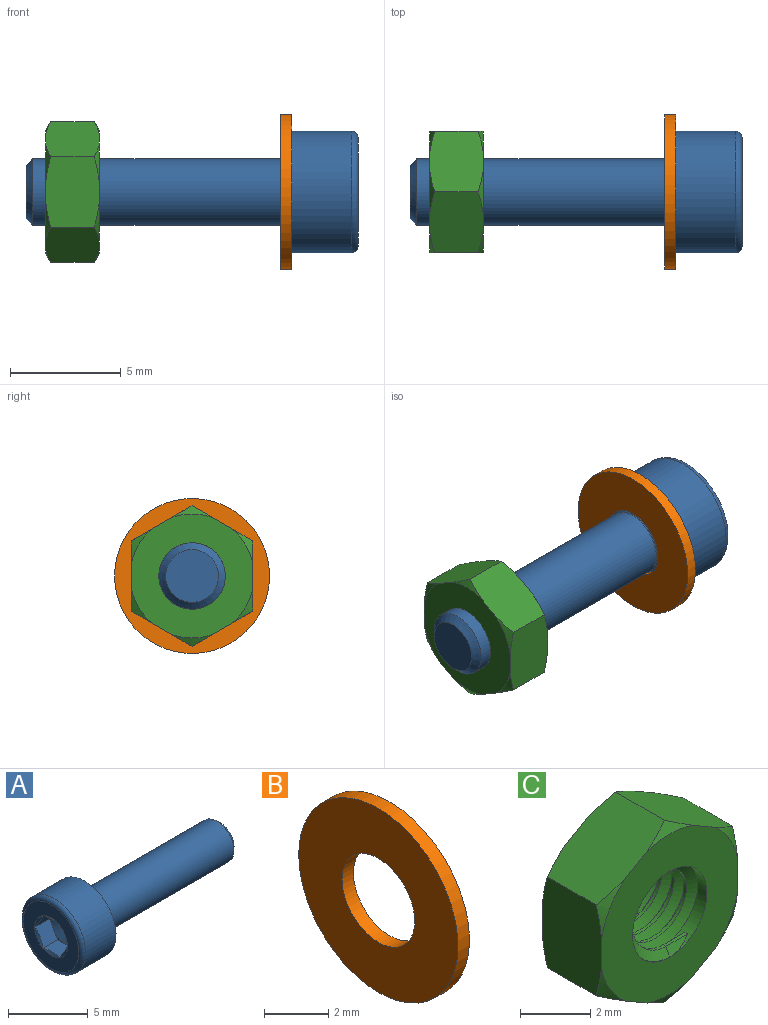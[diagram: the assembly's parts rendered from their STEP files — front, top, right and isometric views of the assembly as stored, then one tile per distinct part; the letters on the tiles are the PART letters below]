
ASSEMBLY  parts=3 mates=2
PART A: 24 faces, bbox 15x6x6 mm
  f0: plane 1.08x0.63mm, normal (-1,0,0), area 0.1mm2, adj f16,f17,f23
  f1: plane 1.25x0.36mm, normal (-1,0,0), area 0.1mm2, adj f17,f18,f23
  f2: plane 1.08x0.63mm, normal (-1,0,0), area 0.1mm2, adj f18,f19,f23
  f3: plane 1.08x0.63mm, normal (-1,0,0), area 0.1mm2, adj f19,f20,f23
  f4: plane 1.25x0.36mm, normal (-1,0,0), area 0.1mm2, adj f20,f21,f23
  f5: cone r=1.45mm half-angle=60deg, axis (-1,0,0), area 1.4mm2, adj f15,f16,f17,f18,f19,f20,f21
  f6: cone r=1.51mm half-angle=26deg, axis (-1,0,0), area 4.6mm2, adj f7,f11
  f7: torus R=1.6mm, axis (1,0,0), area 0.4mm2, adj f6,f10
  f8: plane 2.39x2.39mm, normal (1,0,0), area 4.5mm2, adj f9
  f9: cone r=1.5mm half-angle=45deg, axis (-1,0,0), area 3.7mm2, adj f8,f10
  f10: cylinder r=1.5mm len=11.18mm, axis (1,0,0), area 105.4mm2, adj f7,f9
  f11: torus R=1.8mm, axis (1,0,0), area 1.2mm2, adj f6,f13
  f12: cylinder r=2.75mm len=5.5mm, axis (1,0,0), area 46.7mm2, adj f13,f14
  f13: plane 5.5x5.5mm, normal (1,0,0), area 13.6mm2, adj f11,f12
  f14: torus R=2.45mm, axis (1,0,0), area 7.8mm2, adj f12,f15
  f15: plane 4.9x4.9mm, normal (-1,0,0), area 12.2mm2, adj f5,f14
  f16: plane 1.45x1.3mm, normal (0,0,-1), area 1.8mm2, adj f0,f5,f17,f21,f22
  f17: plane 1.29x1.25mm, normal (0,0.87,-0.5), area 1.8mm2, adj f0,f1,f5,f16,f18
  f18: plane 1.29x1.25mm, normal (0,0.87,0.5), area 1.8mm2, adj f1,f2,f5,f17,f19
  f19: plane 1.45x1.3mm, normal (0,0,1), area 1.8mm2, adj f2,f3,f5,f18,f20
  f20: plane 1.29x1.25mm, normal (0,-0.87,0.5), area 1.8mm2, adj f3,f4,f5,f19,f21
  f21: plane 1.29x1.25mm, normal (0,-0.87,-0.5), area 1.8mm2, adj f4,f5,f16,f20,f22
  f22: plane 1.08x0.63mm, normal (-1,0,0), area 0.1mm2, adj f16,f21,f23
  f23: cone r=1.25mm half-angle=60deg, axis (-1,0,0), area 5.7mm2, adj f0,f1,f2,f3,f4,f22
PART B: 4 faces, bbox 0.5x7x7 mm
  f0: plane 7x7mm, normal (-1,0,0), area 30.4mm2, adj f1,f3
  f1: cylinder r=1.6mm len=3.2mm, axis (1,0,0), area 5mm2, adj f0,f2
  f2: plane 7x7mm, normal (1,0,0), area 30.4mm2, adj f1,f3
  f3: cylinder r=3.5mm len=7mm, axis (1,0,0), area 11mm2, adj f0,f2
PART C: 28 faces, bbox 6.4x2.6x6.5 mm
  f0: cone r=2.8mm half-angle=60deg, axis (0,-1,0), area 0.4mm2, adj f11,f22,f23
  f1: cone r=2.8mm half-angle=60deg, axis (0,-1,0), area 0.4mm2, adj f11,f23,f24
  f2: cone r=2.8mm half-angle=60deg, axis (0,-1,0), area 0.4mm2, adj f11,f24,f25
  f3: cone r=2.8mm half-angle=60deg, axis (0,-1,0), area 0.4mm2, adj f11,f25,f26
  f4: cone r=2.8mm half-angle=60deg, axis (0,-1,0), area 0.4mm2, adj f11,f22,f27
  f5: cone r=3.18mm half-angle=60deg, axis (0,1,0), area 0.4mm2, adj f10,f22,f23
  f6: cone r=3.18mm half-angle=60deg, axis (0,1,0), area 0.4mm2, adj f10,f23,f24
  f7: cone r=3.18mm half-angle=60deg, axis (0,1,0), area 0.4mm2, adj f10,f24,f25
  f8: cone r=3.18mm half-angle=60deg, axis (0,1,0), area 0.4mm2, adj f10,f25,f26
  f9: cone r=3.18mm half-angle=60deg, axis (0,1,0), area 0.4mm2, adj f10,f26,f27
  f10: plane 5.6x5.5mm, normal (0,-1,0), area 17.4mm2, adj f5,f6,f7,f8,f9,f12,f21,f22
  f11: plane 5.6x5.5mm, normal (0,1,0), area 17.4mm2, adj f0,f1,f2,f3,f4,f12,f20,f22
  f12: cylinder r=1.5mm len=3mm, axis (0,1,0), area 6mm2, adj f10,f11,f13,f15,f16,f17,f18,f19
  f13: plane 0.44x0.25mm, normal (-0.88,0,-0.48), area 0.1mm2, adj f12,f14,f15,f16
  f14: cylinder r=1.21mm len=2.43mm, axis (0,1,0), area 3.3mm2, adj f13,f15,f16,f17
  f15: bspline ~3.46x3mm, area 11mm2, adj f12,f13,f14,f18
  f16: bspline ~3.46x3mm, area 11mm2, adj f12,f13,f14,f19
  f17: plane 0.88x0.11mm, normal (0,0,1), area 0.1mm2, adj f12,f14,f18,f19
  f18: plane 0.96x0.37mm, normal (0,0.87,0.5), area 0.2mm2, adj f12,f15,f17
  f19: plane 0.96x0.37mm, normal (0,-0.87,0.5), area 0.2mm2, adj f12,f16,f17
  f20: cone r=2.8mm half-angle=60deg, axis (0,-1,0), area 0.4mm2, adj f11,f26,f27
  f21: cone r=3.18mm half-angle=60deg, axis (0,1,0), area 0.4mm2, adj f10,f22,f27
  f22: plane 2.87x2.52mm, normal (-0.5,0,0.87), area 7.2mm2, adj f0,f4,f5,f10,f11,f21,f23,f27
  f23: plane 2.87x2.52mm, normal (0.5,0,0.87), area 7.2mm2, adj f0,f1,f5,f6,f10,f11,f22,f24
  f24: plane 3.3x2.52mm, normal (1,0,0), area 7.2mm2, adj f1,f2,f6,f7,f10,f11,f23,f25
  f25: plane 2.87x2.52mm, normal (0.5,0,-0.87), area 7.2mm2, adj f2,f3,f7,f8,f10,f11,f24,f26
  f26: plane 2.87x2.52mm, normal (-0.5,0,-0.87), area 7.2mm2, adj f3,f8,f9,f10,f11,f20,f25,f27
  f27: plane 3.3x2.52mm, normal (-1,0,0), area 7.2mm2, adj f4,f9,f10,f11,f20,f21,f22,f26
PLACE A rot(axis=(0,1,0),180deg) t=(0.5,0,0)mm
PLACE B at identity fixed
PLACE C rot(axis=(0,0,1),90deg) t=(-10.6,0,0)mm
MATE fastened A.f5 <-> B.f1  axis (-1,0,0) through (0.5,0,0)mm
MATE fastened C.f0 <-> B.f1  axis (-1,0,0) through (-8.2,0,0)mm
